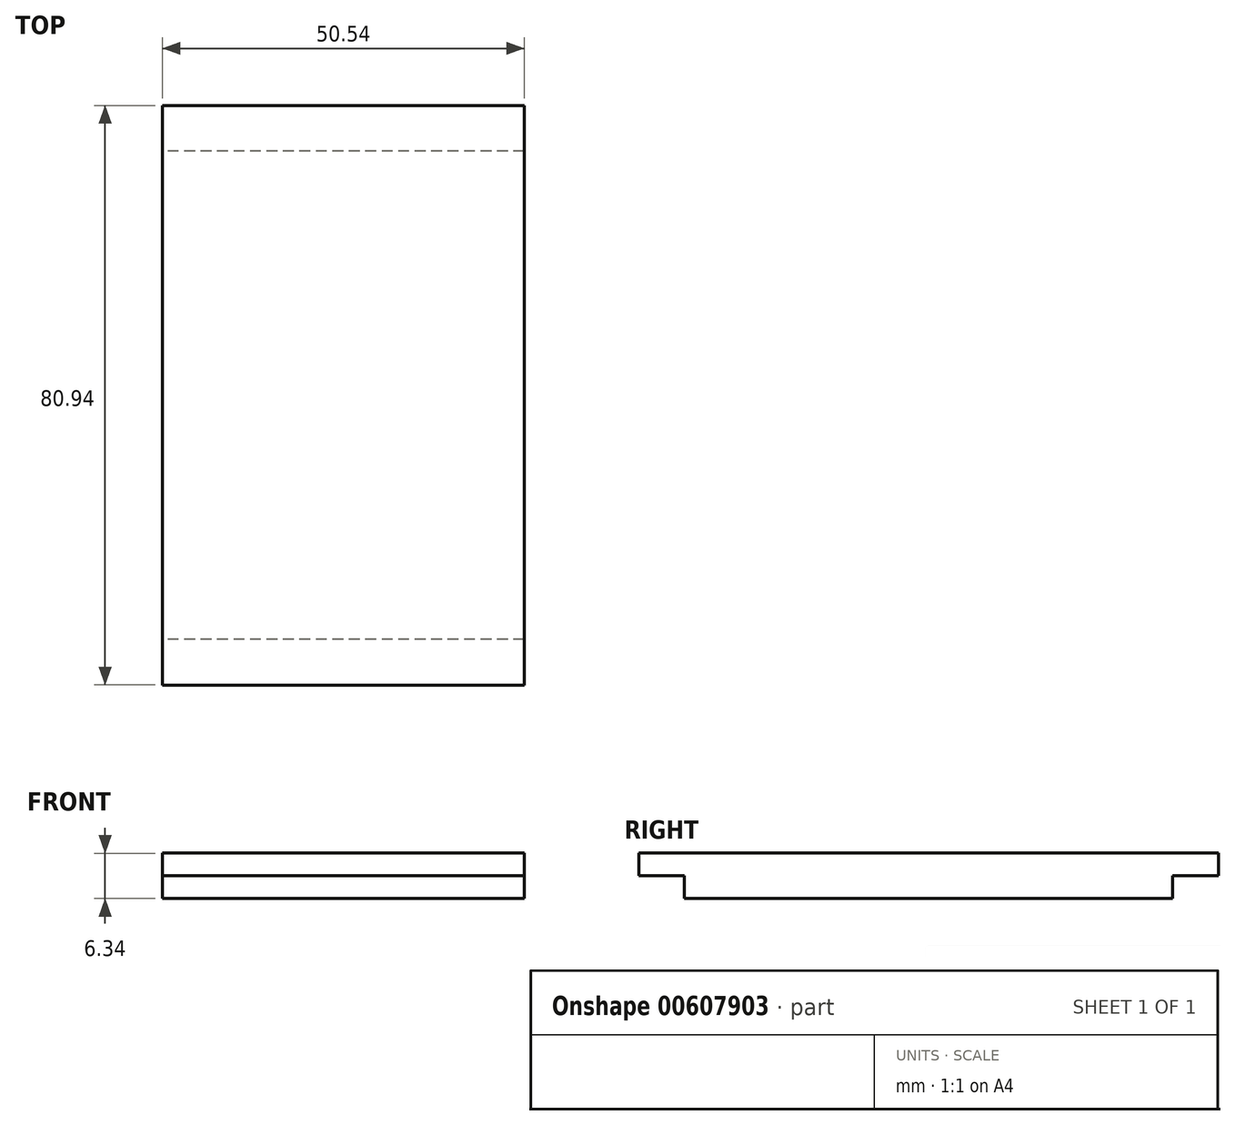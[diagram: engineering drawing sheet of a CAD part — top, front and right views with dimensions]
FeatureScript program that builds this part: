
annotation { "Feature Type Name" : "Feature", "Feature Type Description" : "" }
export const myFeature = defineFeature(function(context is Context, id is Id, definition is map)
    precondition{}
    {
        {
            var Q0;
            Q0=qCreatedBy(makeId("Top.planeOp"),FACE);
            var sketch = newSketch(context, id + "F0", { "sketchPlane" : qUnion([Q0])});
            skLineSegment(sketch, "E0.bottom", {"start": v(25.27, 40.47) * mm, "end": v(-25.27, 40.47) * mm});
            skLineSegment(sketch, "E0.top", {"start": v(25.27, -40.47) * mm, "end": v(-25.27, -40.47) * mm});
            skLineSegment(sketch, "E0.left", {"start": v(25.27, 40.47) * mm, "end": v(25.27, -40.47) * mm});
            skLineSegment(sketch, "E0.right", {"start": v(-25.27, 40.47) * mm, "end": v(-25.27, -40.47) * mm});
            skPoint(sketch, "E0.middle", {"position": v(0, 0) * mm});
            skLineSegment(sketch, "E1.0", {"start": v(25.53, -34.1) * mm, "end": v(-25.53, -34.1) * mm});
            skLineSegment(sketch, "E2.0", {"start": v(25.78, 34.1) * mm, "end": v(-25.27, 34.1) * mm});
            skSolve(sketch);
        }
        {
            var Q0;
            Q0=makeQuery(id+"F0.imprint","IMPRINT",FACE,{"disambiguationData":[TD([[makeQuery(id+"F0.imprint","IMPRINT",EDGE,{"derivedFrom":sQuery(id+"F0.wireOp",EDGE,"E0.bottom")}),1.0]])]});
            var Q1;
            {var subQ0=sQuery(id+"F0.wireOp",EDGE,"E1.0");Q1=makeQuery(id+"F0.imprint","IMPRINT",FACE,{"disambiguationData":[TD([[makeQuery(id+"F0.imprint","IMPRINT",EDGE,{"derivedFrom":subQ0}),-1.0]])]});}
            var Q2;
            {var subQ0=sQuery(id+"F0.wireOp",EDGE,"E0.top");Q2=makeQuery(id+"F0.imprint","IMPRINT",FACE,{"disambiguationData":[TD([[makeQuery(id+"F0.imprint","IMPRINT",EDGE,{"derivedFrom":subQ0}),-1.0]])]});}
            extrude(context, id + "F1", {"entities" : qUnion([Q0, Q1, Q2]), "depth" : 3.17 * mm, "offsetDistance" : 25.4 * mm});
        }
        {
            var Q0;
            {var subQ0=sQuery(id+"F0.wireOp",EDGE,"E1.0");Q0=makeQuery(id+"F0.imprint","IMPRINT",FACE,{"disambiguationData":[TD([[makeQuery(id+"F0.imprint","IMPRINT",EDGE,{"derivedFrom":subQ0}),-1.0]])]});}
            extrude(context, id + "F2", {"entities" : qUnion([Q0]), "operationType" : NewBodyOperationType.ADD, "oppositeDirection" : true, "depth" : 3.17 * mm, "offsetDistance" : 25.4 * mm});
        }
    });
